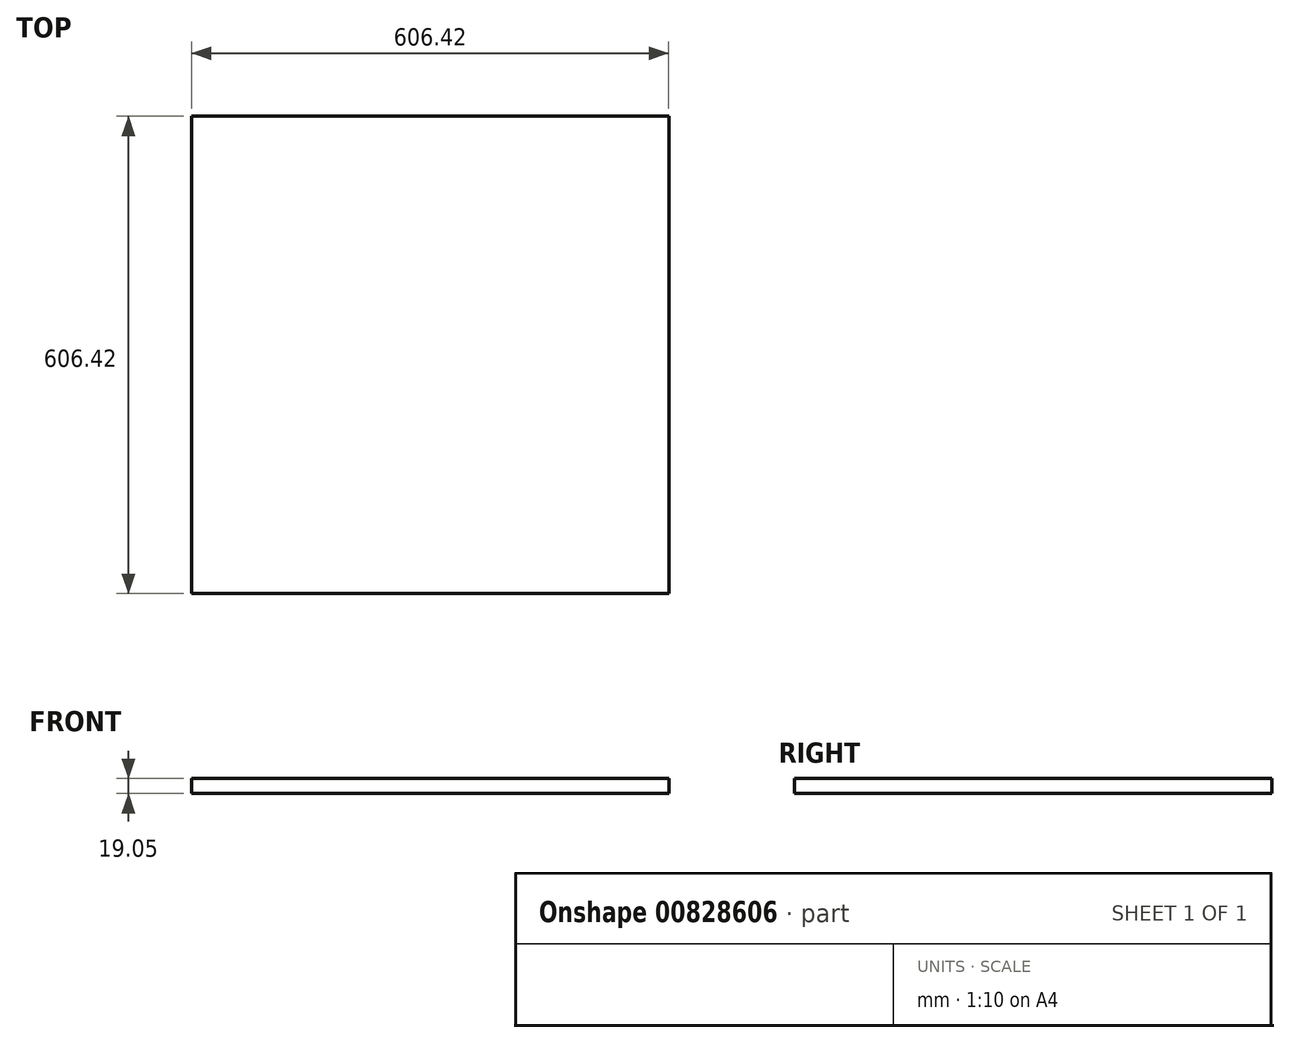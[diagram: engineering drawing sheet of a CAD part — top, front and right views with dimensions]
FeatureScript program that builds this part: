
annotation { "Feature Type Name" : "Feature", "Feature Type Description" : "" }
export const myFeature = defineFeature(function(context is Context, id is Id, definition is map)
    precondition{}
    {
        {
            var Q0;
            Q0=qCreatedBy(makeId("Top.planeOp"),FACE);
            var sketch = newSketch(context, id + "F0", { "sketchPlane" : qUnion([Q0])});
            skLineSegment(sketch, "E0.bottom", {"start": v(-293.84, -303.21) * mm, "end": v(312.58, -303.21) * mm});
            skLineSegment(sketch, "E0.top", {"start": v(-293.84, 303.21) * mm, "end": v(312.58, 303.21) * mm});
            skLineSegment(sketch, "E0.left", {"start": v(-293.84, -303.21) * mm, "end": v(-293.84, 303.21) * mm});
            skLineSegment(sketch, "E0.right", {"start": v(312.58, -303.21) * mm, "end": v(312.58, 303.21) * mm});
            skPoint(sketch, "E0.middle", {"position": v(9.37, 0) * mm});
            skSolve(sketch);
        }
        {
            var Q0;
            Q0=makeQuery(id+"F0.imprint","IMPRINT",FACE,{"disambiguationData":[TD([[makeQuery(id+"F0.imprint","IMPRINT",EDGE,{"derivedFrom":sQuery(id+"F0.wireOp",EDGE,"E0.bottom")}),1.0]])]});
            extrude(context, id + "F1", {"entities" : qUnion([Q0]), "depth" : 19.05 * mm, "offsetDistance" : 25.4 * mm});
        }
    });
